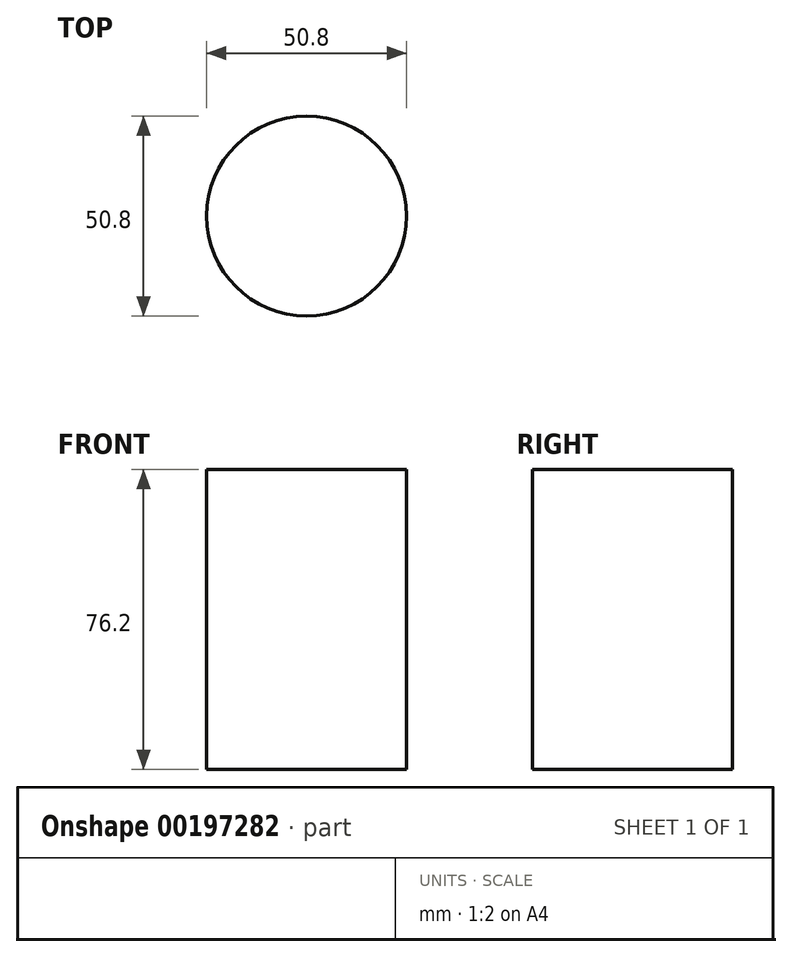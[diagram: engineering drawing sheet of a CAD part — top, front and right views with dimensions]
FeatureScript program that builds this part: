
annotation { "Feature Type Name" : "Feature", "Feature Type Description" : "" }
export const myFeature = defineFeature(function(context is Context, id is Id, definition is map)
    precondition{}
    {
        {
            var Q0;
            Q0=qCreatedBy(makeId("Top.planeOp"),FACE);
            var sketch = newSketch(context, id + "F0", { "sketchPlane" : qUnion([Q0])});
            skCircle(sketch, "E0", {"center": v(0, 0) * mm, "radius": 25.4 * mm});
            skSolve(sketch);
        }
        {
            var Q0;
            Q0 = qSketchRegion(id + "F0", true);
            extrude(context, id + "F1", {"entities" : qUnion([Q0]), "depth" : 76.2 * mm});
        }
    });
